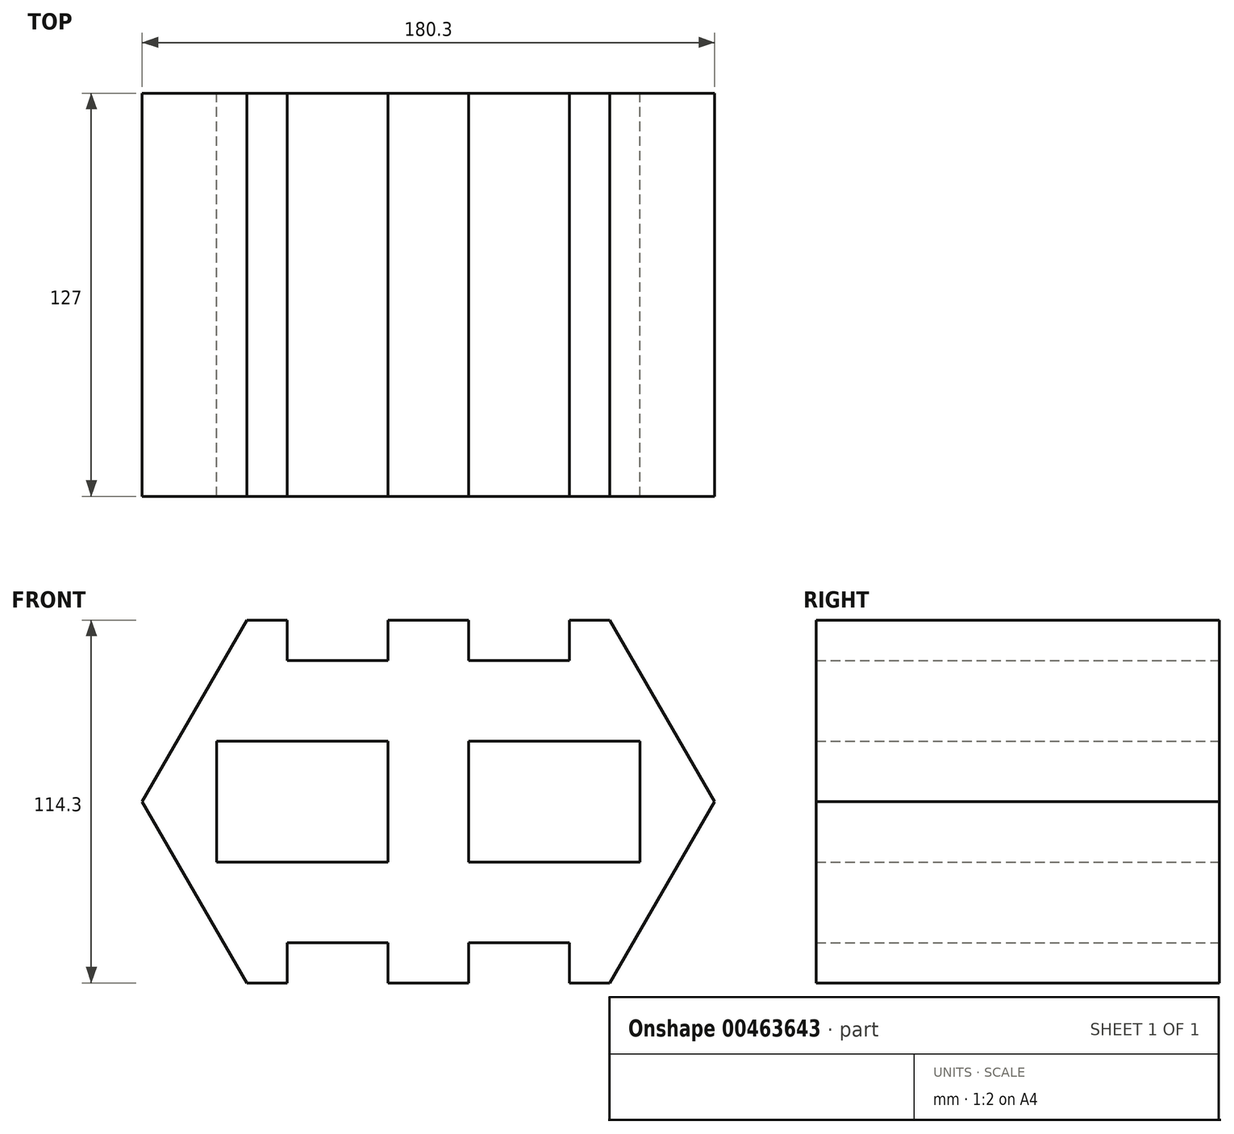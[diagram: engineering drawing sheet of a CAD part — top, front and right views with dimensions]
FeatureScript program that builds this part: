
annotation { "Feature Type Name" : "Feature", "Feature Type Description" : "" }
export const myFeature = defineFeature(function(context is Context, id is Id, definition is map)
    precondition{}
    {
        {
            var Q0;
            Q0=qCreatedBy(makeId("Front.planeOp"),FACE);
            var sketch = newSketch(context, id + "F0", { "sketchPlane" : qUnion([Q0])});
            skLineSegment(sketch, "E0", {"start": v(0, 0) * mm, "end": v(12.7, 0) * mm});
            skLineSegment(sketch, "E1", {"start": v(0, 0) * mm, "end": v(-33, -57.15) * mm});
            skLineSegment(sketch, "E2", {"start": v(12.7, 0) * mm, "end": v(12.7, -12.7) * mm});
            skLineSegment(sketch, "E3", {"start": v(12.7, -12.7) * mm, "end": v(44.45, -12.7) * mm});
            skLineSegment(sketch, "E4", {"start": v(44.45, -12.7) * mm, "end": v(44.45, 0) * mm});
            skLineSegment(sketch, "E5", {"start": v(44.45, 0) * mm, "end": v(69.85, 0) * mm});
            skLineSegment(sketch, "E6", {"start": v(69.85, 0) * mm, "end": v(69.85, -12.7) * mm});
            skLineSegment(sketch, "E7", {"start": v(69.85, -12.7) * mm, "end": v(101.6, -12.7) * mm});
            skLineSegment(sketch, "E8", {"start": v(101.6, -12.7) * mm, "end": v(101.6, 0) * mm});
            skLineSegment(sketch, "E9", {"start": v(101.6, 0) * mm, "end": v(114.3, 0) * mm});
            skLineSegment(sketch, "E10", {"start": v(114.3, 0) * mm, "end": v(147.3, -57.15) * mm});
            skLineSegment(sketch, "E11", {"start": v(-33, -57.15) * mm, "end": v(0, -114.3) * mm});
            skLineSegment(sketch, "E12", {"start": v(0, -114.3) * mm, "end": v(12.7, -114.3) * mm});
            skLineSegment(sketch, "E13", {"start": v(12.7, -114.3) * mm, "end": v(12.7, -101.6) * mm});
            skLineSegment(sketch, "E14", {"start": v(12.7, -101.6) * mm, "end": v(44.45, -101.6) * mm});
            skLineSegment(sketch, "E15", {"start": v(44.45, -101.6) * mm, "end": v(44.45, -114.3) * mm});
            skLineSegment(sketch, "E16", {"start": v(44.45, -114.3) * mm, "end": v(69.85, -114.3) * mm});
            skLineSegment(sketch, "E17", {"start": v(69.85, -114.3) * mm, "end": v(69.85, -101.6) * mm});
            skLineSegment(sketch, "E18", {"start": v(69.85, -101.6) * mm, "end": v(101.6, -101.6) * mm});
            skLineSegment(sketch, "E19", {"start": v(101.6, -101.6) * mm, "end": v(101.6, -114.3) * mm});
            skLineSegment(sketch, "E20", {"start": v(101.6, -114.3) * mm, "end": v(114.3, -114.3) * mm});
            skLineSegment(sketch, "E21", {"start": v(114.3, -114.3) * mm, "end": v(147.3, -57.15) * mm});
            skLineSegment(sketch, "E22.bottom", {"start": v(44.45, -38.1) * mm, "end": v(-9.53, -38.1) * mm});
            skLineSegment(sketch, "E22.top", {"start": v(44.45, -76.2) * mm, "end": v(-9.52, -76.2) * mm});
            skLineSegment(sketch, "E22.left", {"start": v(44.45, -38.1) * mm, "end": v(44.45, -76.2) * mm});
            skLineSegment(sketch, "E22.right", {"start": v(-9.53, -38.1) * mm, "end": v(-9.52, -76.2) * mm});
            skLineSegment(sketch, "E23", {"start": v(69.85, 0) * mm, "end": v(69.85, -38.1) * mm});
            skLineSegment(sketch, "E24", {"start": v(69.85, -38.1) * mm, "end": v(123.83, -38.1) * mm});
            skLineSegment(sketch, "E25", {"start": v(123.83, -38.1) * mm, "end": v(123.83, -76.2) * mm});
            skLineSegment(sketch, "E26", {"start": v(123.83, -76.2) * mm, "end": v(69.85, -76.2) * mm});
            skLineSegment(sketch, "E27", {"start": v(69.85, -76.2) * mm, "end": v(69.85, -38.1) * mm});
            skSolve(sketch);
        }
        {
            var Q0;
            Q0=makeQuery(id+"F0.imprint","IMPRINT",FACE,{"disambiguationData":[TD([[makeQuery(id+"F0.imprint","IMPRINT",EDGE,{"derivedFrom":sQuery(id+"F0.wireOp",EDGE,"E0")}),-1.0]])]});
            extrude(context, id + "F1", {"entities" : qUnion([Q0]), "depth" : 127 * mm});
        }
    });
